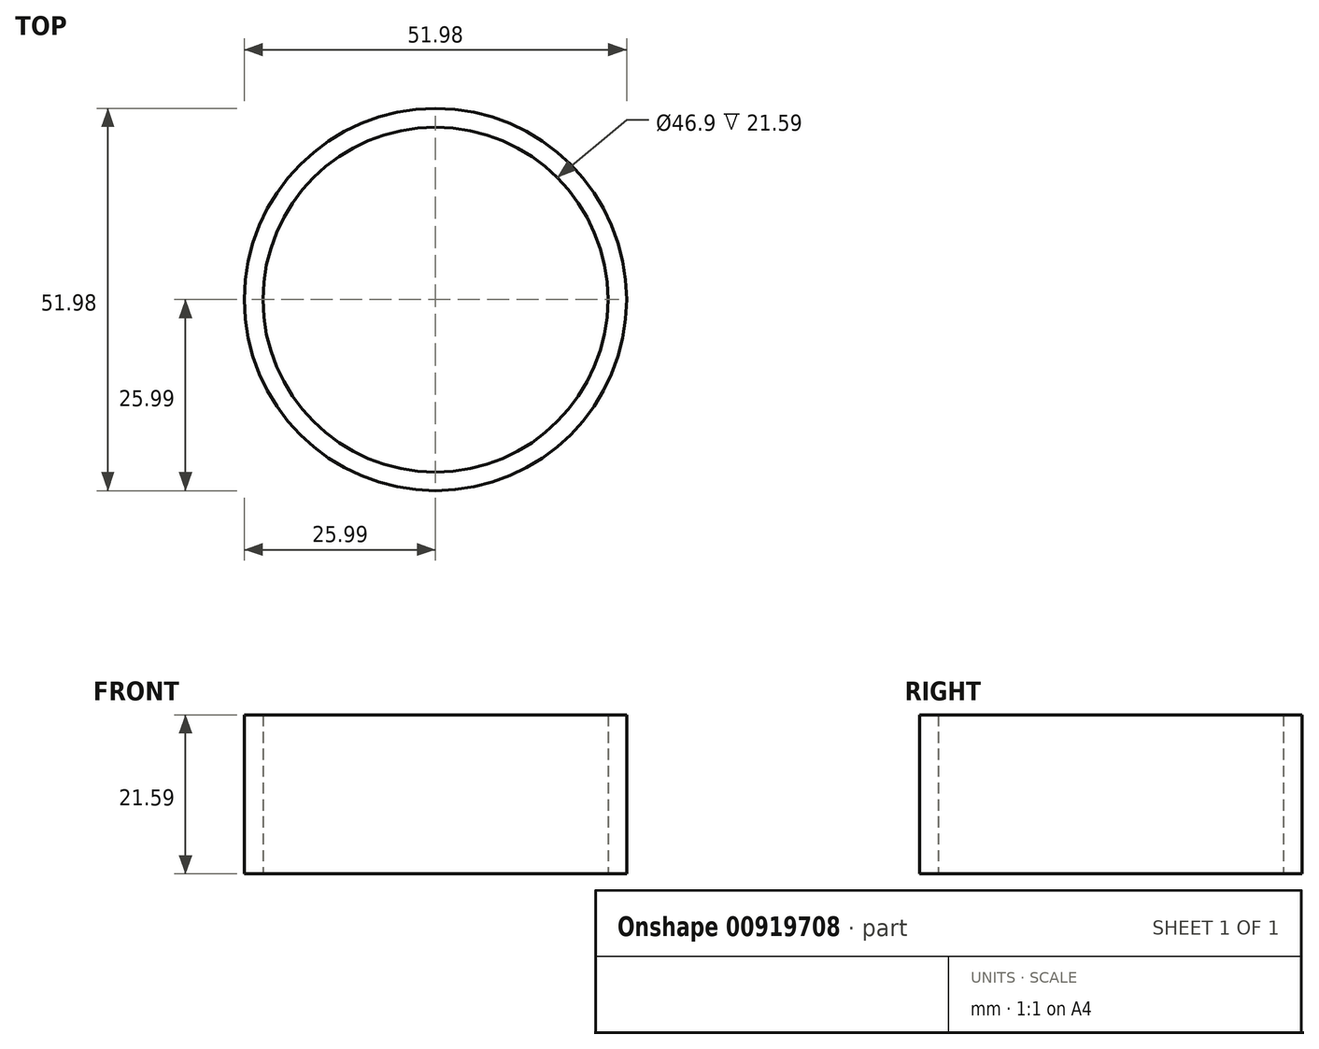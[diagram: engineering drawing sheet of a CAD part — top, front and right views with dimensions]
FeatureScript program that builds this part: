
annotation { "Feature Type Name" : "Feature", "Feature Type Description" : "" }
export const myFeature = defineFeature(function(context is Context, id is Id, definition is map)
    precondition{}
    {
        {
            var Q0;
            Q0=qCreatedBy(makeId("Top.planeOp"),FACE);
            var sketch = newSketch(context, id + "F0", { "sketchPlane" : qUnion([Q0])});
            skCircle(sketch, "E0", {"center": v(0, 0) * mm, "radius": 25.99 * mm});
            skSolve(sketch);
        }
        {
            var Q0;
            Q0=makeQuery(id+"F0.imprint","IMPRINT",FACE,{"disambiguationData":[TD([[makeQuery(id+"F0.imprint","IMPRINT",EDGE,{"derivedFrom":sQuery(id+"F0.wireOp",EDGE,"E0")}),1.0]])]});
            var sketch = newSketch(context, id + "F1", { "sketchPlane" : qUnion([Q0])});
            skSolve(sketch);
        }
        {
            var Q0;
            Q0=makeQuery(id+"F1.imprint","IMPRINT",FACE,{"disambiguationData":[TD([[makeQuery(id+"F1.imprint","IMPRINT",EDGE,{"derivedFrom":makeQuery(id+"F0.imprint","IMPRINT",EDGE,{"derivedFrom":sQuery(id+"F0.wireOp",EDGE,"E0")})}),1.0]])]});
            var sketch = newSketch(context, id + "F2", { "sketchPlane" : qUnion([Q0])});
            skCircle(sketch, "E1.0", {"center": v(0, 0) * mm, "radius": 23.45 * mm});
            skSolve(sketch);
        }
        {
            var Q0;
            Q0=makeQuery(id+"F0.imprint","IMPRINT",FACE,{"disambiguationData":[TD([[makeQuery(id+"F0.imprint","IMPRINT",EDGE,{"derivedFrom":sQuery(id+"F0.wireOp",EDGE,"E0")}),1.0]])]});
            extrude(context, id + "F3", {"entities" : qUnion([Q0]), "depth" : 21.59 * mm, "offsetDistance" : 25.4 * mm});
        }
        {
            var Q0;
            Q0=makeQuery(id+"F2.imprint","IMPRINT",FACE,{"disambiguationData":[TD([[makeQuery(id+"F2.imprint","IMPRINT",EDGE,{"derivedFrom":sQuery(id+"F2.wireOp",EDGE,"E1.0")}),1.0]])]});
            extrude(context, id + "F4", {"entities" : qUnion([Q0]), "operationType" : NewBodyOperationType.REMOVE, "endBound" : BoundingType.THROUGH_ALL, "depth" : 25.4 * mm, "offsetDistance" : 25.4 * mm});
        }
    });
